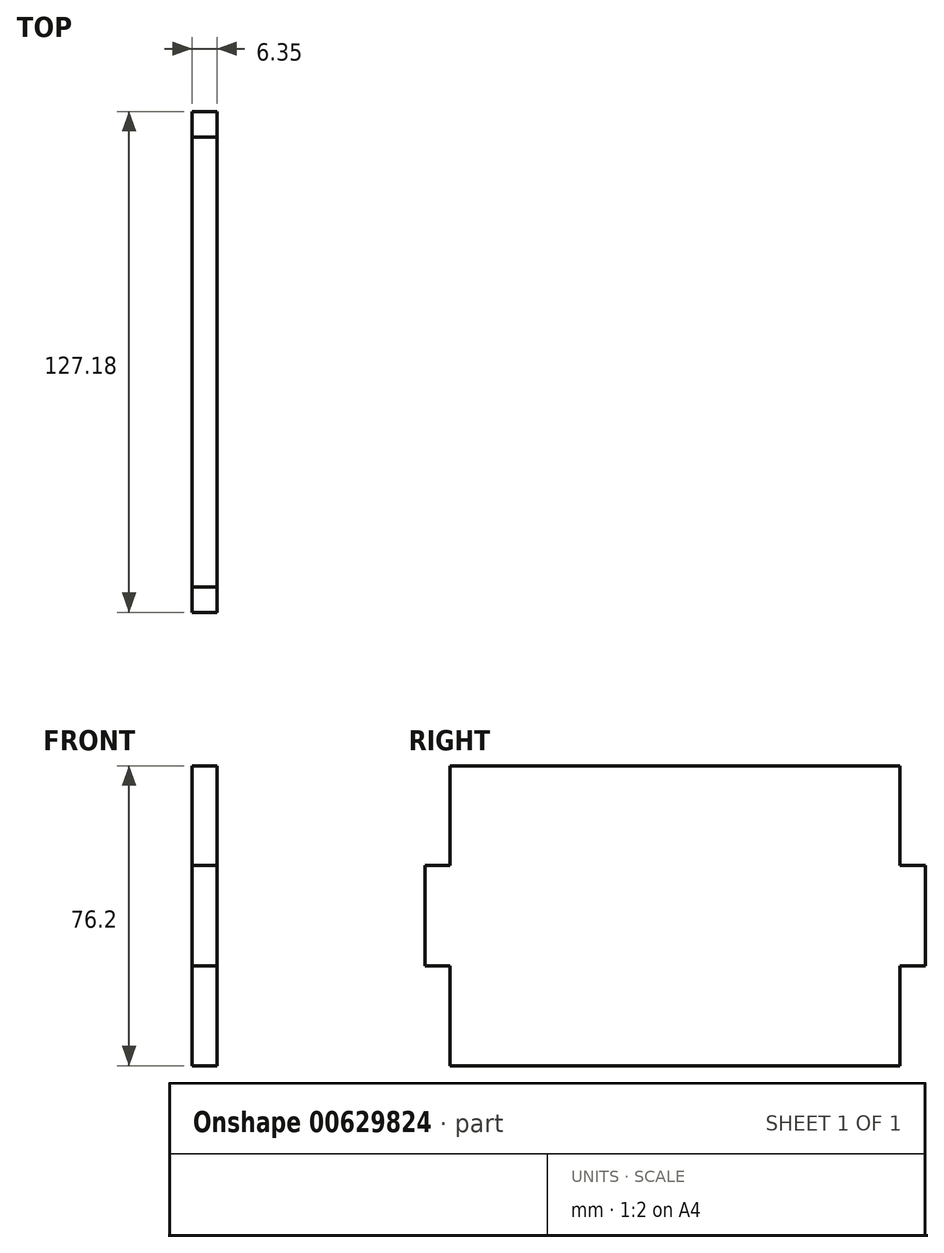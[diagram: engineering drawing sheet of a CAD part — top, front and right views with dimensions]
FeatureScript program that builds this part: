
annotation { "Feature Type Name" : "Feature", "Feature Type Description" : "" }
export const myFeature = defineFeature(function(context is Context, id is Id, definition is map)
    precondition{}
    {
        {
            var Q0;
            Q0=qCreatedBy(makeId("Right.planeOp"),FACE);
            var sketch = newSketch(context, id + "F0", { "sketchPlane" : qUnion([Q0])});
            skLineSegment(sketch, "E0.bottom", {"start": v(0, 0) * mm, "end": v(114.3, 0) * mm});
            skLineSegment(sketch, "E0.top", {"start": v(0, 76.2) * mm, "end": v(114.3, 76.2) * mm});
            skLineSegment(sketch, "E0.left", {"start": v(0, 0) * mm, "end": v(0, 76.2) * mm});
            skLineSegment(sketch, "E0.right", {"start": v(114.3, 0) * mm, "end": v(114.3, 76.2) * mm});
            skLineSegment(sketch, "E1.bottom", {"start": v(-6.44, 50.89) * mm, "end": v(0, 50.89) * mm});
            skLineSegment(sketch, "E1.top", {"start": v(-6.44, 25.31) * mm, "end": v(0, 25.31) * mm});
            skLineSegment(sketch, "E1.left", {"start": v(-6.44, 50.89) * mm, "end": v(-6.44, 25.31) * mm});
            skLineSegment(sketch, "E1.right", {"start": v(0, 50.89) * mm, "end": v(0, 25.31) * mm});
            skLineSegment(sketch, "E2.bottom", {"start": v(114.3, 50.89) * mm, "end": v(120.74, 50.89) * mm});
            skLineSegment(sketch, "E2.top", {"start": v(114.3, 25.31) * mm, "end": v(120.74, 25.31) * mm});
            skLineSegment(sketch, "E2.left", {"start": v(114.3, 50.89) * mm, "end": v(114.3, 25.31) * mm});
            skLineSegment(sketch, "E2.right", {"start": v(120.74, 50.89) * mm, "end": v(120.74, 25.31) * mm});
            skLineSegment(sketch, "E3.bottom", {"start": v(18.96, 0) * mm, "end": v(44.54, 0) * mm});
            skLineSegment(sketch, "E3.top", {"start": v(18.96, -6.44) * mm, "end": v(44.54, -6.44) * mm});
            skLineSegment(sketch, "E3.left", {"start": v(18.96, 0) * mm, "end": v(18.96, -6.44) * mm});
            skLineSegment(sketch, "E3.right", {"start": v(44.54, 0) * mm, "end": v(44.54, -6.44) * mm});
            skLineSegment(sketch, "E4.bottom", {"start": v(69.76, 0) * mm, "end": v(95.34, 0) * mm});
            skLineSegment(sketch, "E4.top", {"start": v(69.76, -6.44) * mm, "end": v(95.34, -6.44) * mm});
            skLineSegment(sketch, "E4.left", {"start": v(69.76, 0) * mm, "end": v(69.76, -6.44) * mm});
            skLineSegment(sketch, "E4.right", {"start": v(95.34, 0) * mm, "end": v(95.34, -6.44) * mm});
            skPoint(sketch, "E5", {"position": v(0, 38.1) * mm});
            skPoint(sketch, "E6", {"position": v(114.3, 38.1) * mm});
            skPoint(sketch, "E7", {"position": v(82.55, 0) * mm});
            skPoint(sketch, "E8", {"position": v(31.75, 0) * mm});
            skSolve(sketch);
        }
        {
            var Q0;
            Q0=makeQuery(id+"F0.imprint","IMPRINT",FACE,{"disambiguationData":[TD([[makeQuery(id+"F0.imprint","IMPRINT",EDGE,{"derivedFrom":sQuery(id+"F0.wireOp",EDGE,"E1.bottom")}),-1.0]])]});
            var Q1;
            {var subQ1=sQuery(id+"F0.wireOp",EDGE,"E0.top");Q1=makeQuery(id+"F0.imprint","IMPRINT",FACE,{"disambiguationData":[TD([[makeQuery(id+"F0.imprint","IMPRINT",EDGE,{"derivedFrom":subQ1}),-1.0]])]});}
            var Q2;
            Q2=makeQuery(id+"F0.imprint","IMPRINT",FACE,{"disambiguationData":[TD([[makeQuery(id+"F0.imprint","IMPRINT",EDGE,{"derivedFrom":sQuery(id+"F0.wireOp",EDGE,"E3.bottom")}),-1.0]])]});
            var Q3;
            Q3=makeQuery(id+"F0.imprint","IMPRINT",FACE,{"disambiguationData":[TD([[makeQuery(id+"F0.imprint","IMPRINT",EDGE,{"derivedFrom":sQuery(id+"F0.wireOp",EDGE,"E4.bottom")}),-1.0]])]});
            var Q4;
            Q4=makeQuery(id+"F0.imprint","IMPRINT",FACE,{"disambiguationData":[TD([[makeQuery(id+"F0.imprint","IMPRINT",EDGE,{"derivedFrom":sQuery(id+"F0.wireOp",EDGE,"E2.bottom")}),-1.0]])]});
            extrude(context, id + "F1", {"entities" : qUnion([Q0, Q1, Q2, Q3, Q4]), "depth" : 6.35 * mm, "offsetDistance" : 25.4 * mm});
        }
    });
